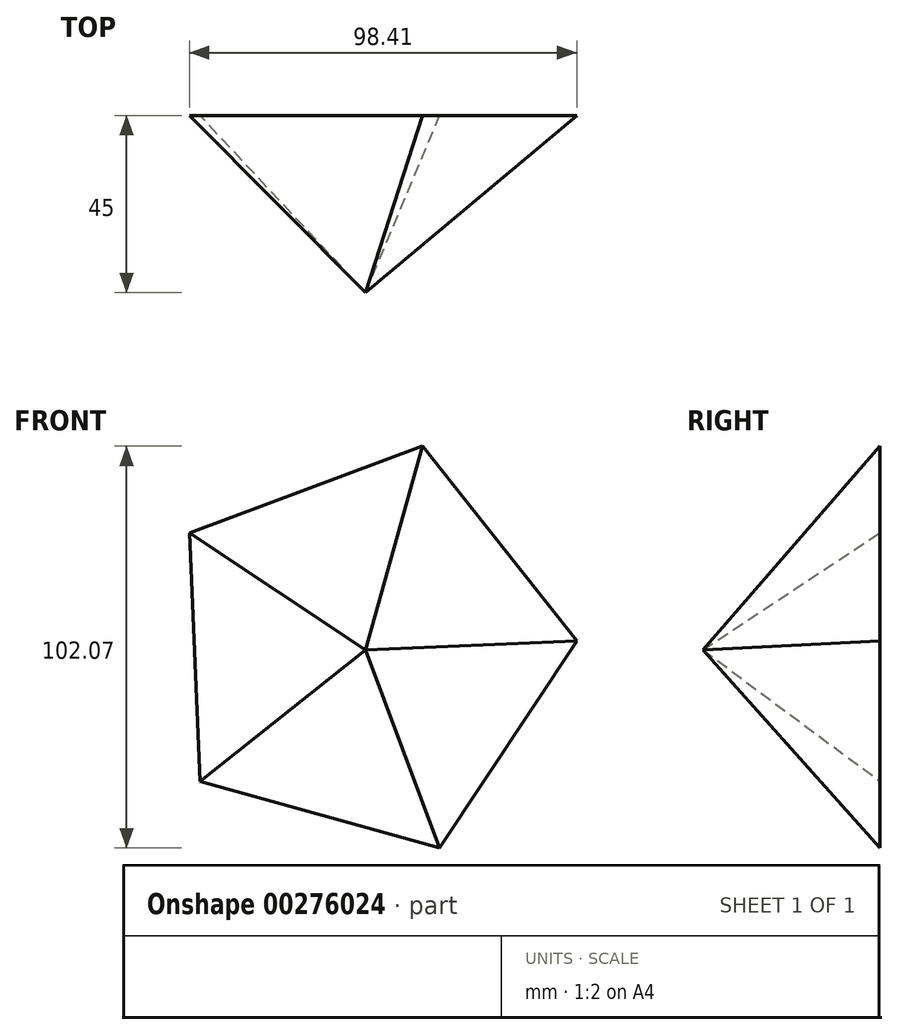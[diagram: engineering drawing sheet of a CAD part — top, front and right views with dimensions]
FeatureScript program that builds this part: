
annotation { "Feature Type Name" : "Feature", "Feature Type Description" : "" }
export const myFeature = defineFeature(function(context is Context, id is Id, definition is map)
    precondition{}
    {
        {
            var Q0;
            Q0=qCreatedBy(makeId("Front.planeOp"),FACE);
            var sketch = newSketch(context, id + "F0", { "sketchPlane" : qUnion([Q0])});
            skCircle(sketch, "E0.cCircle", {"center": v(0, 0) * mm, "radius": 53.7 * mm, "construction": true});
            skLineSegment(sketch, "E0.0", {"start": v(-44.75, 29.7) * mm, "end": v(14.4, 51.74) * mm});
            skLineSegment(sketch, "E0.1", {"start": v(14.4, 51.74) * mm, "end": v(53.66, 2.28) * mm});
            skLineSegment(sketch, "E0.2", {"start": v(53.66, 2.28) * mm, "end": v(18.75, -50.33) * mm});
            skLineSegment(sketch, "E0.3", {"start": v(18.75, -50.33) * mm, "end": v(-42.07, -33.39) * mm});
            skLineSegment(sketch, "E0.4", {"start": v(-42.07, -33.39) * mm, "end": v(-44.75, 29.7) * mm});
            skSolve(sketch);
        }
        {
            var Q0;
            Q0=qCreatedBy(makeId("Front.planeOp"),FACE);
            cPlane(context, id + "F1", {"entities" : qUnion([Q0]), "cplaneType" : CPlaneType.OFFSET, "offset" : 45 * mm, "width" : 150 * mm, "height" : 150 * mm});
        }
        {
            var Q0;
            Q0=qCreatedBy(id+"F1.planeOp",FACE);
            var sketch = newSketch(context, id + "F2", { "sketchPlane" : qUnion([Q0])});
            skPoint(sketch, "E1", {"position": v(0, 0) * mm});
            skSolve(sketch);
        }
        {
            var Q0;
            Q0=sQuery(id+"F2.wireOp",VERTEX,"E1");
            var Q1;
            Q1=makeQuery(id+"F0.imprint","IMPRINT",FACE,{"disambiguationData":[TD([[makeQuery(id+"F0.imprint","IMPRINT",EDGE,{"derivedFrom":sQuery(id+"F0.wireOp",EDGE,"E0.0")}),-1.0]])]});
            loft(context, id + "F3", {"sheetProfilesArray" : [{ "sheetProfileEntities" : qUnion([Q0]) }, { "sheetProfileEntities" : qUnion([Q1]) }]});
        }
    });
